# Revit family: BLAUBERG-KOMFORT_EC_DBE_2000
name_source: partatom
category: Mechanical Equipment
units: mm (PartAtom-declared; Revit-internal decimal feet)

## family parameters
Always vertical = Yes
Classification = None
Cut with Voids When Loaded = No
OmniClass Number = 23.75.35.14
OmniClass Title = Air Handling Units
Part Type = Normal
Room Calculation Point = No
Round Connector Dimension = Use Diameter
Shared = No
Work Plane-Based = No

## types (1)
- KOMFORT EC DBE 2000 S21
    B = 950 mm  [stored 3.1168 ft]
    B1 = 225 mm  [stored 0.738189 ft]
    B2 = 225 mm  [stored 0.738189 ft]
    Bottom Maintenance Zone Height = 600 mm  [stored 1.9685 ft]
    Casing Material = Metal Zinc
    Current = 27 A
    D = 315 mm  [stored 1.03346 ft]
    DPS_B1 = 302 mm  [stored 0.990814 ft]
    DPS_B2 = 292 mm  [stored 0.958005 ft]
    DPS_H = 93 mm  [stored 0.305118 ft]
    Description = Air Handling Unit
    Drain Connection Diameter = 16 mm  [stored 0.0524934 ft]
    DrainD = 16 mm  [stored 0.0524934 ft]
    DrainPipe = Yes
    Duct Connection Diameter = 315 mm  [stored 1.03346 ft]
    Extract Air Filter = G4
    Family Version = 1.0
    H = 762 mm  [stored 2.5 ft]
    H1 = 367 mm  [stored 1.20407 ft]
    HDrainCon = 36 mm  [stored 0.11811 ft]
    HandleB = 100 mm  [stored 0.328084 ft]
    HandleL1 = 250 mm  [stored 0.82021 ft]
    HandleL2 = 450 mm  [stored 1.47638 ft]
    Heat Exchanger Material = aluminium
    Heat Exchanger Type = cross-flow
    Heat recovery efficiency (%) = 50..67
    Heater power = 15000 W
    L = 1400 mm  [stored 4.59318 ft]
    LDrainCon = 35 mm  [stored 0.114829 ft]
    LDrainCon1 = 661 mm  [stored 2.16864 ft]
    LDuctCon = 50 mm  [stored 0.164042 ft]
    Load Classification = HVAC
    Maintenance Zone Material = Maintenance Zone
    Manufacturer = Blauberg
    Maximum Air Flow = 2100 m³/h
    Maximum Unit Current With Electric Heater = 27 A
    Maximum Unit Current Without Electric Heater = 5 A
    Maximum Unit Power Without Electric Heater = 876 W
    Model = KOMFORT EC DBE 2000 S21
    Number of Poles = 3
    Plastic Material = Polypropylene Black
    Power = 15876 W
    Power Factor = 1
    RPM (min-1) = 2920
    SEC Class = NRVU
    Side Maintenance Zone Height = 500 mm  [stored 1.64042 ft]
    Sound Pressure Level at 3 m (dBA) = 36
    Supply Air Filter = G4
    Transported Air Temperature (°C) = -25…+40
    Type Comments = Air Handling Unit KOMFORT EC DBE 2000 S21
    URL = https://blaubergventilatoren.de
    Voltage = 400 V
    Weight = 140.00 kg

note: [stored X ft] marks values corroborated as IEEE doubles in the binary element streams (Revit-internal decimal feet)

## geometry (parser evidence)
native form markers: Sweep x5
no freeform markers — native parametric forms only
